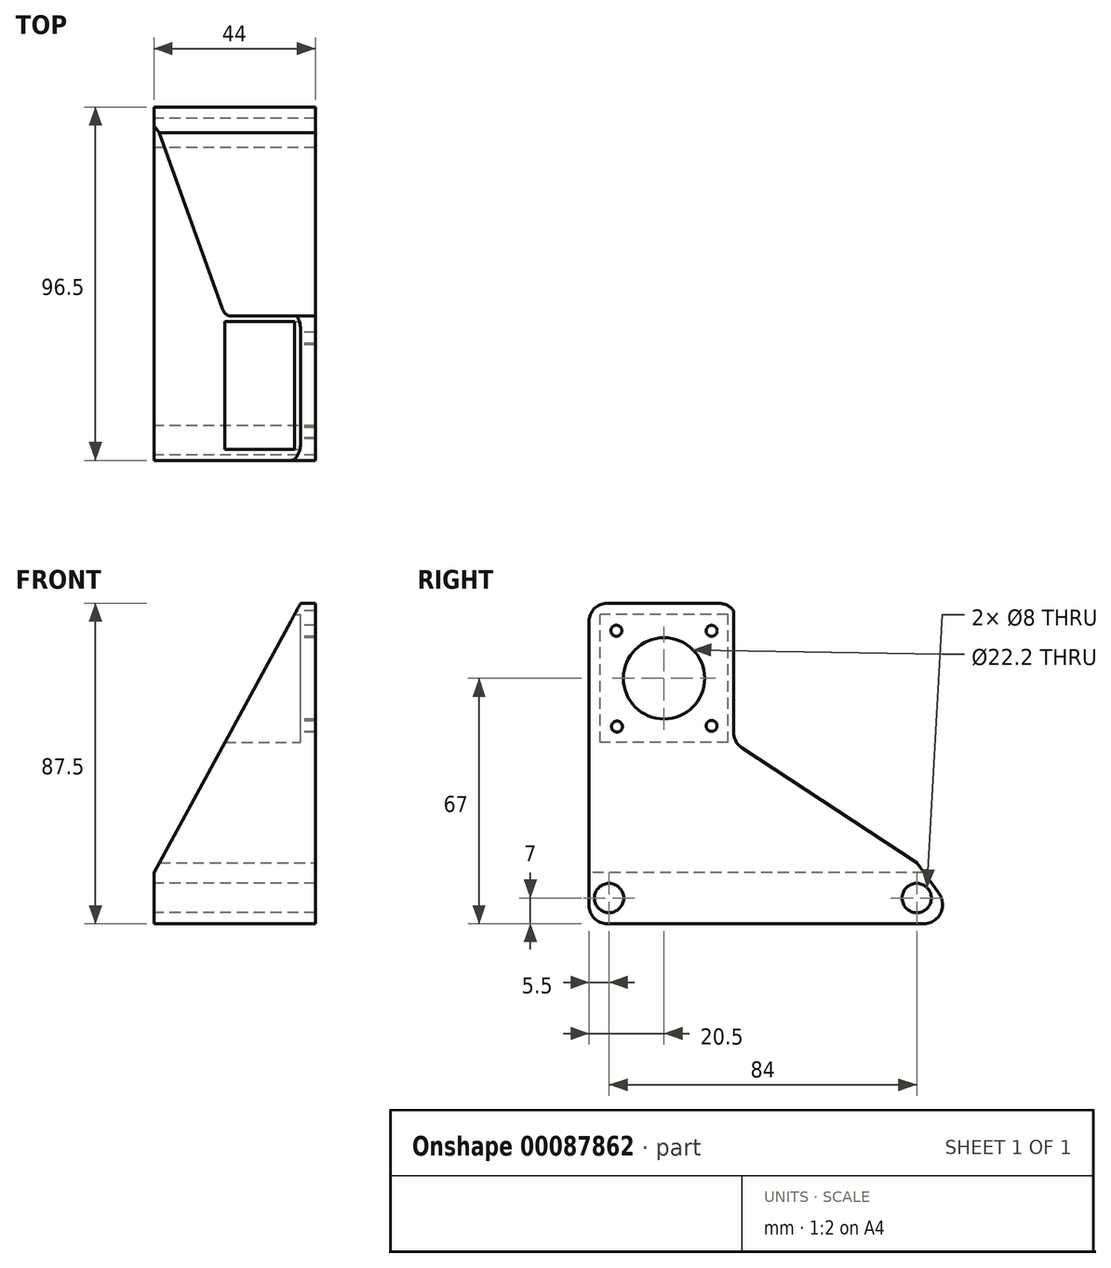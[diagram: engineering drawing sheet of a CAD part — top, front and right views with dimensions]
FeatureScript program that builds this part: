
annotation { "Feature Type Name" : "Feature", "Feature Type Description" : "" }
export const myFeature = defineFeature(function(context is Context, id is Id, definition is map)
    precondition{}
    {
        {
            var Q0;
            Q0=qCreatedBy(makeId("Right.planeOp"),FACE);
            var sketch = newSketch(context, id + "F0", { "sketchPlane" : qUnion([Q0])});
            skCircle(sketch, "E0", {"center": v(0, 0) * mm, "radius": 4 * mm});
            skCircle(sketch, "E1", {"center": v(-84, 0) * mm, "radius": 4 * mm});
            skCircle(sketch, "E2", {"center": v(-69, 60) * mm, "radius": 11.1 * mm});
            skLineSegment(sketch, "E3.bottom", {"start": v(-56, 47) * mm, "end": v(-82, 47) * mm, "construction": true});
            skLineSegment(sketch, "E3.top", {"start": v(-56, 73) * mm, "end": v(-82, 73) * mm, "construction": true});
            skLineSegment(sketch, "E3.left", {"start": v(-56, 47) * mm, "end": v(-56, 73) * mm, "construction": true});
            skLineSegment(sketch, "E3.right", {"start": v(-82, 47) * mm, "end": v(-82, 73) * mm, "construction": true});
            skLineSegment(sketch, "E4.bottom", {"start": v(-51.5, 42.5) * mm, "end": v(-86.5, 42.5) * mm});
            skLineSegment(sketch, "E4.top", {"start": v(-51.5, 77.5) * mm, "end": v(-86.5, 77.5) * mm});
            skLineSegment(sketch, "E4.left", {"start": v(-51.5, 42.5) * mm, "end": v(-51.5, 77.5) * mm});
            skLineSegment(sketch, "E4.right", {"start": v(-86.5, 42.5) * mm, "end": v(-86.5, 77.5) * mm});
            skCircle(sketch, "E5", {"center": v(-82, 73) * mm, "radius": 1.5 * mm});
            skCircle(sketch, "E6", {"center": v(-56, 72.98) * mm, "radius": 1.5 * mm});
            skCircle(sketch, "E7", {"center": v(-56, 47) * mm, "radius": 1.5 * mm});
            skCircle(sketch, "E8", {"center": v(-81.85, 46.83) * mm, "radius": 1.5 * mm});
            skLineSegment(sketch, "E9.bottom", {"start": v(-89.5, 80.5) * mm, "end": v(-51.5, 80.5) * mm});
            skLineSegment(sketch, "E9.top", {"start": v(-89.5, -7) * mm, "end": v(7, -7) * mm});
            skLineSegment(sketch, "E9.left", {"start": v(-89.5, 80.5) * mm, "end": v(-89.5, -7) * mm});
            skLineSegment(sketch, "E9.right", {"start": v(7, 0) * mm, "end": v(7, -7) * mm});
            skLineSegment(sketch, "E10", {"start": v(-51.5, 80.5) * mm, "end": v(7, 0) * mm});
            skSolve(sketch);
        }
        {
            var Q0;
            Q0=makeQuery(id+"F0.imprint","IMPRINT",FACE,{"disambiguationData":[TD([[makeQuery(id+"F0.imprint","IMPRINT",EDGE,{"derivedFrom":sQuery(id+"F0.wireOp",EDGE,"E0")}),-1.0]])]});
            var Q1;
            Q1=makeQuery(id+"F0.imprint","IMPRINT",FACE,{"disambiguationData":[TD([[makeQuery(id+"F0.imprint","IMPRINT",EDGE,{"derivedFrom":sQuery(id+"F0.wireOp",EDGE,"E2")}),-1.0]])]});
            extrude(context, id + "F1", {"entities" : qUnion([Q0, Q1]), "depth" : 4 * mm});
        }
        {
            var Q0;
            Q0=makeQuery(id+"F0.imprint","IMPRINT",FACE,{"disambiguationData":[TD([[makeQuery(id+"F0.imprint","IMPRINT",EDGE,{"derivedFrom":sQuery(id+"F0.wireOp",EDGE,"E0")}),-1.0]])]});
            extrude(context, id + "F2", {"entities" : qUnion([Q0]), "operationType" : NewBodyOperationType.ADD, "oppositeDirection" : true, "depth" : 40 * mm});
        }
        {
            var Q0;
            {var subQ0=sQuery(id+"F0.wireOp",EDGE,"E9.left");Q0=makeQuery(id+"F2.boolean.opBoolean","MERGE",FACE,{"derivedFrom":[makeQuery(id+"F1.opExtrude","SWEPT_FACE",FACE,{"disambiguationData":[OSD([subQ0])]}),makeQuery(id+"F2.opExtrude","SWEPT_FACE",FACE,{"disambiguationData":[OSD([subQ0])]})]});}
            var sketch = newSketch(context, id + "F3", { "sketchPlane" : qUnion([Q0])});
            skLineSegment(sketch, "E11", {"start": v(0, 80.5) * mm, "end": v(-40, 7) * mm});
            skLineSegment(sketch, "E12.0", {"start": v(-40, 4) * mm, "end": v(-40, -4) * mm});
            skSolve(sketch);
        }
        {
            var Q0;
            {var subQ0=sQuery(id+"F3.wireOp",EDGE,"E11");Q0=makeQuery(id+"F3.imprint","IMPRINT",FACE,{"disambiguationData":[TD([[makeQuery(id+"F3.imprint","IMPRINT",EDGE,{"derivedFrom":subQ0}),-1.0]])]});}
            extrude(context, id + "F4", {"entities" : qUnion([Q0]), "operationType" : NewBodyOperationType.REMOVE, "endBound" : BoundingType.THROUGH_ALL, "oppositeDirection" : true, "depth" : 25 * mm});
        }
        {
            var Q0;
            {var subQ0=sQuery(id+"F0.wireOp",EDGE,"E9.left");var subQ1=sQuery(id+"F0.wireOp",EDGE,"E9.top");Q0=makeQuery(id+"F2.boolean.opBoolean","MERGE",EDGE,{"derivedFrom":[makeQuery(id+"F1.opExtrude","SWEPT_EDGE",EDGE,{"disambiguationData":[OSD([subQ1,subQ0])]}),makeQuery(id+"F2.opExtrude","SWEPT_EDGE",EDGE,{"disambiguationData":[OSD([subQ1,subQ0])]})]});}
            var Q1;
            {var subQ0=sQuery(id+"F0.wireOp",EDGE,"E9.right");var subQ1=sQuery(id+"F0.wireOp",EDGE,"E9.top");Q1=makeQuery(id+"F2.boolean.opBoolean","MERGE",EDGE,{"derivedFrom":[makeQuery(id+"F1.opExtrude","SWEPT_EDGE",EDGE,{"disambiguationData":[OSD([subQ1,subQ0])]}),makeQuery(id+"F2.opExtrude","SWEPT_EDGE",EDGE,{"disambiguationData":[OSD([subQ1,subQ0])]})]});}
            var Q2;
            {var subQ0=sQuery(id+"F0.wireOp",EDGE,"E10");var subQ1=sQuery(id+"F0.wireOp",EDGE,"E9.right");Q2=makeQuery(id+"F2.boolean.opBoolean","MERGE",EDGE,{"derivedFrom":[makeQuery(id+"F1.opExtrude","SWEPT_EDGE",EDGE,{"disambiguationData":[OSD([subQ1,subQ0])]}),makeQuery(id+"F2.opExtrude","SWEPT_EDGE",EDGE,{"disambiguationData":[OSD([subQ1,subQ0])]})]});}
            var Q3;
            {var subQ0=sQuery(id+"F0.wireOp",EDGE,"E9.left");var subQ1=sQuery(id+"F0.wireOp",EDGE,"E9.bottom");Q3=makeQuery(id+"F2.boolean.opBoolean","MERGE",EDGE,{"derivedFrom":[makeQuery(id+"F1.opExtrude","SWEPT_EDGE",EDGE,{"disambiguationData":[OSD([subQ1,subQ0])]}),makeQuery(id+"F2.opExtrude","SWEPT_EDGE",EDGE,{"disambiguationData":[OSD([subQ1,subQ0])]})]});}
            var Q4;
            {var subQ0=sQuery(id+"F0.wireOp",EDGE,"E10");var subQ1=sQuery(id+"F0.wireOp",EDGE,"E9.bottom");Q4=makeQuery(id+"F2.boolean.opBoolean","MERGE",EDGE,{"derivedFrom":[makeQuery(id+"F1.opExtrude","SWEPT_EDGE",EDGE,{"disambiguationData":[OSD([subQ1,subQ0])]}),makeQuery(id+"F2.opExtrude","SWEPT_EDGE",EDGE,{"disambiguationData":[OSD([subQ1,subQ0])]})]});}
            fillet(context, id + "F5", {"entities" : qUnion([Q0, Q1, Q2, Q3, Q4]), "radius" : 5 * mm, "tangentPropagation" : true, "allowEdgeOverflow" : false});
        }
        {
            var Q0;
            Q0=makeQuery(id+"F1.opExtrude","CAP_FACE",FACE,{"disambiguationData":[OSD([sQuery(id+"F0.wireOp",EDGE,"E0"),sQuery(id+"F0.wireOp",EDGE,"E1"),sQuery(id+"F0.wireOp",EDGE,"E2"),sQuery(id+"F0.wireOp",EDGE,"E5"),sQuery(id+"F0.wireOp",EDGE,"E6"),sQuery(id+"F0.wireOp",EDGE,"E7"),sQuery(id+"F0.wireOp",EDGE,"E8"),sQuery(id+"F0.wireOp",EDGE,"E9.bottom"),sQuery(id+"F0.wireOp",EDGE,"E9.top"),sQuery(id+"F0.wireOp",EDGE,"E9.left"),sQuery(id+"F0.wireOp",EDGE,"E9.right"),sQuery(id+"F0.wireOp",EDGE,"E10")])],"isStart":false});
            var sketch = newSketch(context, id + "F6", { "sketchPlane" : qUnion([Q0])});
            skLineSegment(sketch, "E13", {"start": v(-50, 78.44) * mm, "end": v(-50, 42.5) * mm});
            skLineSegment(sketch, "E14", {"start": v(-50, 42.5) * mm, "end": v(-23.89, 42.5) * mm});
            skLineSegment(sketch, "E15.0", {"start": v(-51.5, 42.5) * mm, "end": v(-86.5, 42.5) * mm});
            skSolve(sketch);
        }
        {
            var Q0;
            {var subQ0=sQuery(id+"F6.wireOp",EDGE,"E13");Q0=makeQuery(id+"F6.imprint","IMPRINT",FACE,{"disambiguationData":[TD([[makeQuery(id+"F6.imprint","IMPRINT",EDGE,{"derivedFrom":subQ0}),1.0]])]});}
            extrude(context, id + "F7", {"entities" : qUnion([Q0]), "operationType" : NewBodyOperationType.REMOVE, "endBound" : BoundingType.THROUGH_ALL, "oppositeDirection" : true, "depth" : 25 * mm});
        }
        {
            var Q0;
            Q0=makeQuery(id+"F6.imprint","IMPRINT",FACE,{"disambiguationData":[TD([[makeQuery(id+"F6.imprint","IMPRINT",EDGE,{"derivedFrom":sQuery(id+"F6.wireOp",EDGE,"E13")}),-1.0]])]});
            var sketch = newSketch(context, id + "F8", { "sketchPlane" : qUnion([Q0])});
            skCircle(sketch, "E16.0", {"center": v(0, 0) * mm, "radius": 4 * mm});
            skLineSegment(sketch, "E17.0", {"start": v(-51.5, 80.5) * mm, "end": v(7, 0) * mm});
            skLineSegment(sketch, "E18", {"start": v(-50, 42.5) * mm, "end": v(0, 9.63) * mm});
            skLineSegment(sketch, "E19.0", {"start": v(-50, 42.5) * mm, "end": v(-23.89, 42.5) * mm});
            skSolve(sketch);
        }
        {
            var Q0;
            {var subQ2=sQuery(id+"F8.wireOp",EDGE,"E18");Q0=makeQuery(id+"F8.imprint","IMPRINT",FACE,{"disambiguationData":[TD([[makeQuery(id+"F8.imprint","IMPRINT",EDGE,{"derivedFrom":subQ2}),1.0]])]});}
            extrude(context, id + "F9", {"entities" : qUnion([Q0]), "operationType" : NewBodyOperationType.REMOVE, "endBound" : BoundingType.THROUGH_ALL, "oppositeDirection" : true, "depth" : 25 * mm});
        }
        {
            var Q0;
            {var subQ0=sQuery(id+"F6.wireOp",EDGE,"E13");Q0=makeQuery(id+"F9.boolean.opBoolean","MERGE",EDGE,{"derivedFrom":[makeQuery(id+"F7.boolean.opBoolean","COPY",EDGE,{"derivedFrom":makeQuery(id+"F7.opExtrude","SWEPT_EDGE",EDGE,{"disambiguationData":[OSD([subQ0,sQuery(id+"F6.wireOp",EDGE,"E14")])]})}),makeQuery(id+"F9.opExtrude","SWEPT_EDGE",EDGE,{"disambiguationData":[OSD([subQ0,sQuery(id+"F8.wireOp",EDGE,"E18"),sQuery(id+"F8.wireOp",EDGE,"E19.0")])]})]});}
            var Q1;
            Q1=makeQuery(id+"F9.boolean.opBoolean","COPY",EDGE,{"derivedFrom":makeQuery(id+"F9.opExtrude","SWEPT_EDGE",EDGE,{"disambiguationData":[OSD([sQuery(id+"F8.wireOp",EDGE,"E17.0"),sQuery(id+"F8.wireOp",EDGE,"E18")])]})});
            fillet(context, id + "F10", {"entities" : qUnion([Q0, Q1]), "radius" : 5 * mm, "tangentPropagation" : true, "allowEdgeOverflow" : false});
        }
    });
